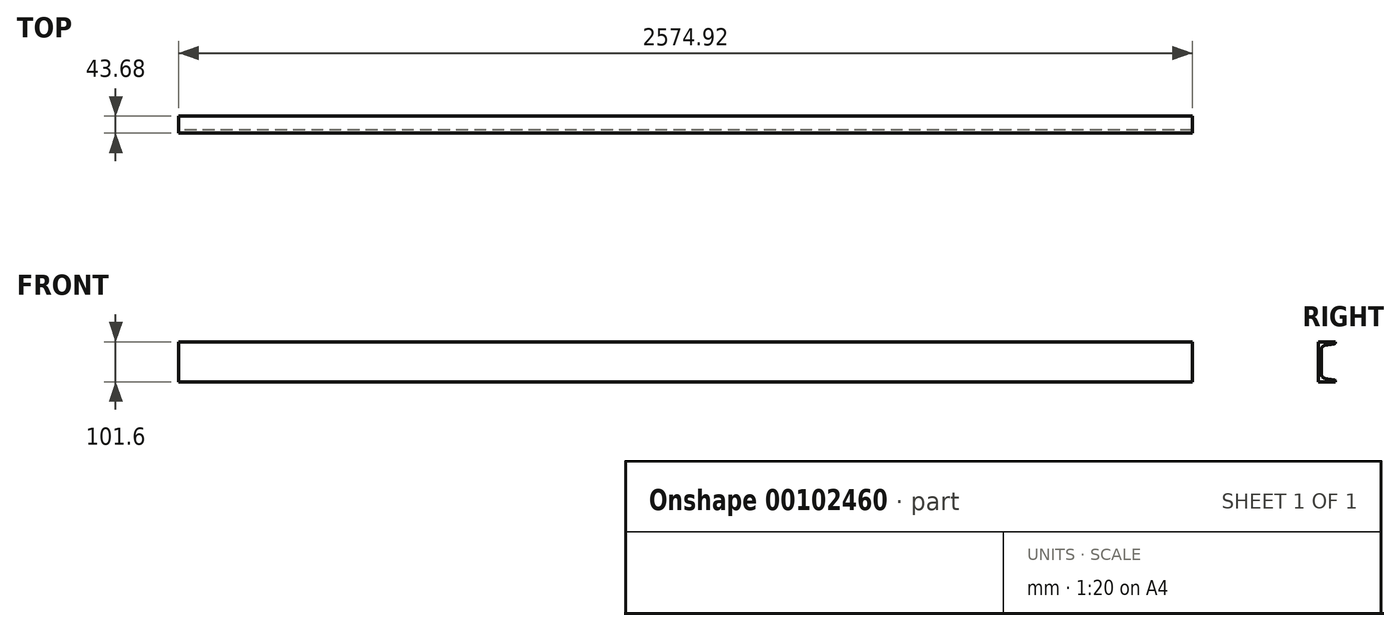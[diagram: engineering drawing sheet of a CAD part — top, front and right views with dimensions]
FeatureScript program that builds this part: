
annotation { "Feature Type Name" : "Feature", "Feature Type Description" : "" }
export const myFeature = defineFeature(function(context is Context, id is Id, definition is map)
    precondition{}
    {
        {
            var Q0;
            Q0=qCreatedBy(makeId("Right.planeOp"),FACE);
            var sketch = newSketch(context, id + "F0", { "sketchPlane" : qUnion([Q0])});
            skLineSegment(sketch, "E0", {"start": v(21.84, 50.8) * mm, "end": v(21.84, 48.6) * mm});
            skArc(sketch, "E1", {"start": v(21.84, 48.6) * mm, "mid": v(21.23, 46.93) * mm, "end": v(19.68, 46.03) * mm});
            skArc(sketch, "E2", {"start": v(-5.42, 41.6) * mm, "mid": v(-11.35, 38.18) * mm, "end": v(-13.7, 31.75) * mm, "construction": true});
            skArc(sketch, "E3", {"start": v(-13.7, -31.75) * mm, "mid": v(-11.35, -38.18) * mm, "end": v(-5.42, -41.6) * mm, "construction": true});
            skArc(sketch, "E4", {"start": v(19.68, -46.03) * mm, "mid": v(21.23, -46.93) * mm, "end": v(21.84, -48.6) * mm, "construction": true});
            skLineSegment(sketch, "E5", {"start": v(-21.84, 50.8) * mm, "end": v(21.84, 50.8) * mm});
            skLineSegment(sketch, "E6", {"start": v(-21.84, 50.8) * mm, "end": v(-21.84, -50.8) * mm});
            skLineSegment(sketch, "E7", {"start": v(-21.84, -50.8) * mm, "end": v(21.84, -50.8) * mm});
            skLineSegment(sketch, "E8", {"start": v(21.84, -50.8) * mm, "end": v(21.84, -48.6) * mm});
            skArc(sketch, "E9", {"start": v(21.84, -48.6) * mm, "mid": v(21.23, -46.93) * mm, "end": v(19.68, -46.03) * mm});
            skLineSegment(sketch, "E10", {"start": v(19.68, -46.03) * mm, "end": v(-5.42, -41.6) * mm});
            skArc(sketch, "E11", {"start": v(-5.42, -41.6) * mm, "mid": v(-11.35, -38.18) * mm, "end": v(-13.7, -31.75) * mm, "construction": true});
            skLineSegment(sketch, "E12", {"start": v(-13.7, -31.75) * mm, "end": v(-13.7, 31.75) * mm});
            skArc(sketch, "E13", {"start": v(-5.42, -41.6) * mm, "mid": v(-11.35, -38.18) * mm, "end": v(-13.7, -31.75) * mm});
            skArc(sketch, "E14", {"start": v(-13.7, 31.75) * mm, "mid": v(-11.35, 38.18) * mm, "end": v(-5.42, 41.6) * mm});
            skLineSegment(sketch, "E15", {"start": v(-5.42, 41.6) * mm, "end": v(19.68, 46.03) * mm});
            skSolve(sketch);
        }
        {
            var Q0;
            Q0 = qSketchRegion(id + "F0", true);
            extrude(context, id + "F1", {"entities" : qUnion([Q0]), "depth" : 2574.92 * mm});
        }
    });
